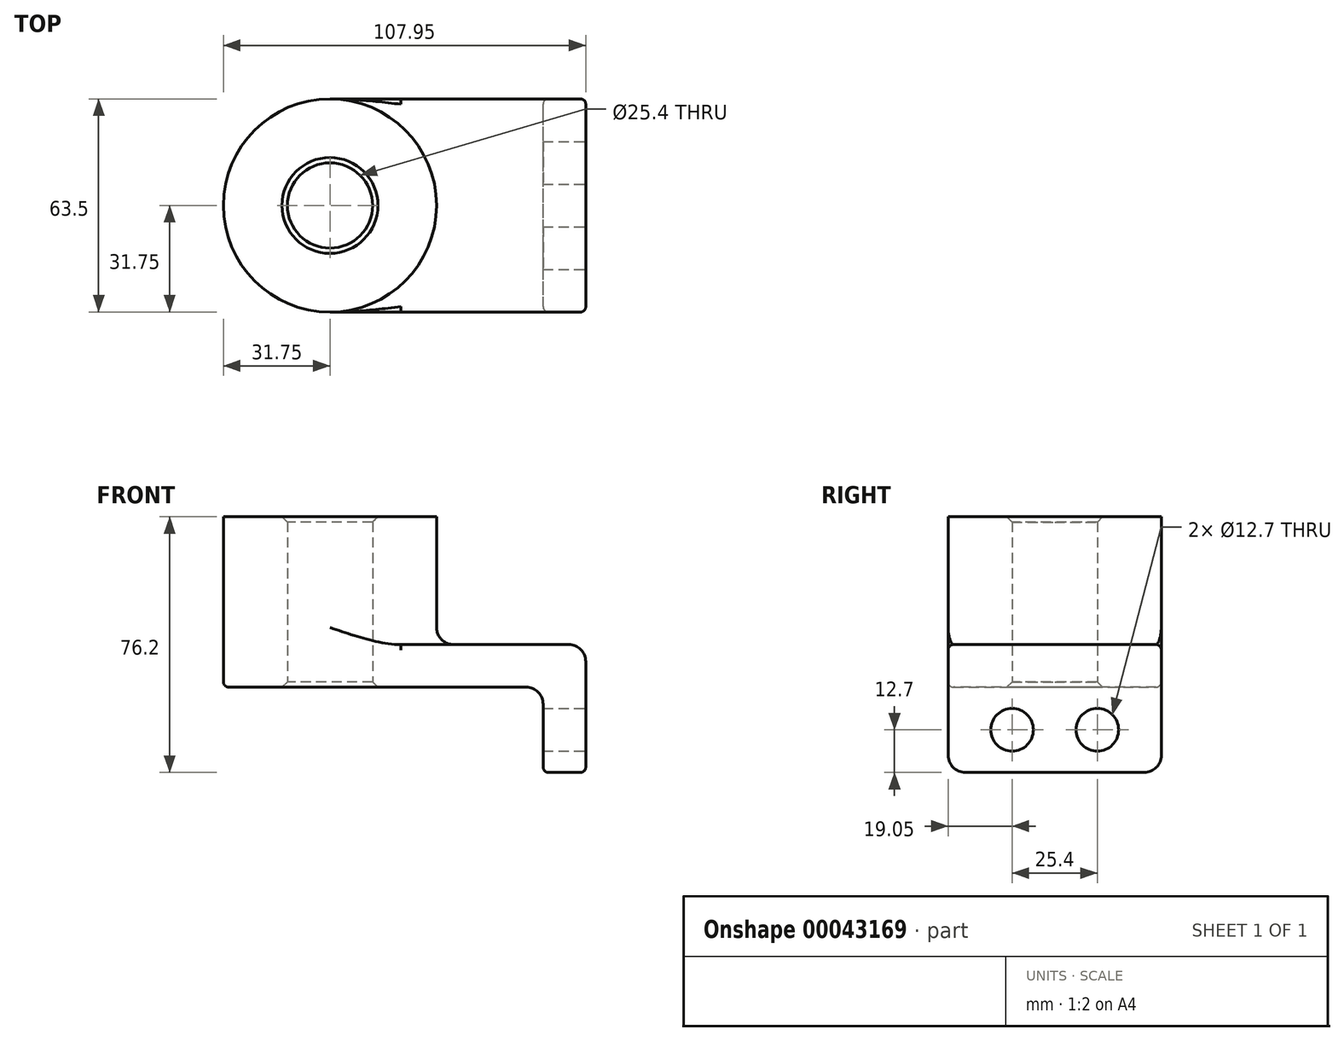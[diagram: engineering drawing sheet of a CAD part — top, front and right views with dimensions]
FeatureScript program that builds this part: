
annotation { "Feature Type Name" : "Feature", "Feature Type Description" : "" }
export const myFeature = defineFeature(function(context is Context, id is Id, definition is map)
    precondition{}
    {
        {
            var Q0;
            Q0=qCreatedBy(makeId("Top.planeOp"),FACE);
            var sketch = newSketch(context, id + "F0", { "sketchPlane" : qUnion([Q0])});
            skLineSegment(sketch, "E0.rect.bottom", {"start": v(-38.1, 31.75) * mm, "end": v(38.1, 31.75) * mm});
            skLineSegment(sketch, "E0.rect.top", {"start": v(-38.1, -31.75) * mm, "end": v(38.1, -31.75) * mm});
            skLineSegment(sketch, "E0.rect.left", {"start": v(-38.1, 31.75) * mm, "end": v(-38.1, -31.75) * mm});
            skLineSegment(sketch, "E0.rect.right", {"start": v(38.1, 31.75) * mm, "end": v(38.1, -31.75) * mm});
            skPoint(sketch, "E0.rect.middle", {"position": v(0, 0) * mm});
            skCircle(sketch, "E1", {"center": v(-38.1, 0) * mm, "radius": 31.75 * mm});
            skCircle(sketch, "E2", {"center": v(-38.1, 0) * mm, "radius": 12.7 * mm});
            skSolve(sketch);
        }
        {
            var Q0;
            Q0 = qSketchRegion(id + "F0", true);
            extrude(context, id + "F1", {"entities" : qUnion([Q0]), "depth" : 12.7 * mm});
        }
        {
            var Q0;
            {var subQ0=sQuery(id+"F0.wireOp",EDGE,"E2");var subQ1=sQuery(id+"F0.wireOp",EDGE,"E0.rect.left");var subQ3=makeQuery(id+"F0.imprint","INTERSECT",VERTEX,{"disambiguationData":[OD(0.0)],"derivedFrom":[subQ1,subQ0]});Q0=makeQuery(id+"F0.imprint","IMPRINT",FACE,{"disambiguationData":[TD([[makeQuery(id+"F0.imprint","IMPRINT",EDGE,{"disambiguationData":[TD([[subQ3,-1.0]])],"derivedFrom":subQ0}),-1.0]])]});}
            var Q1;
            {var subQ0=sQuery(id+"F0.wireOp",EDGE,"E2");var subQ1=sQuery(id+"F0.wireOp",EDGE,"E0.rect.left");var subQ3=makeQuery(id+"F0.imprint","INTERSECT",VERTEX,{"disambiguationData":[OD(0.0)],"derivedFrom":[subQ1,subQ0]});Q1=makeQuery(id+"F0.imprint","IMPRINT",FACE,{"disambiguationData":[TD([[makeQuery(id+"F0.imprint","IMPRINT",EDGE,{"disambiguationData":[TD([[subQ3,1.0]])],"derivedFrom":subQ0}),-1.0]])]});}
            extrude(context, id + "F2", {"entities" : qUnion([Q0, Q1]), "operationType" : NewBodyOperationType.ADD, "depth" : 50.8 * mm});
        }
        {
            var Q0;
            Q0=makeQuery(id+"F1.opExtrude","SWEPT_FACE",FACE,{"disambiguationData":[OSD([sQuery(id+"F0.wireOp",EDGE,"E0.rect.right")])]});
            var sketch = newSketch(context, id + "F3", { "sketchPlane" : qUnion([Q0])});
            skLineSegment(sketch, "E3.bottom", {"start": v(-31.75, 12.7) * mm, "end": v(31.75, 12.7) * mm});
            skLineSegment(sketch, "E3.top", {"start": v(-31.75, -25.4) * mm, "end": v(31.75, -25.4) * mm});
            skLineSegment(sketch, "E3.left", {"start": v(-31.75, 12.7) * mm, "end": v(-31.75, -25.4) * mm});
            skLineSegment(sketch, "E3.right", {"start": v(31.75, 12.7) * mm, "end": v(31.75, -25.4) * mm});
            skCircle(sketch, "E4", {"center": v(-12.7, -12.7) * mm, "radius": 6.35 * mm});
            skLineSegment(sketch, "E5", {"start": v(0, 0) * mm, "end": v(0, -25.4) * mm});
            skCircle(sketch, "E6.MirrorC", {"center": v(12.7, -12.7) * mm, "radius": 6.35 * mm});
            skSolve(sketch);
        }
        {
            var Q0;
            Q0 = qSketchRegion(id + "F3", true);
            extrude(context, id + "F4", {"entities" : qUnion([Q0]), "operationType" : NewBodyOperationType.ADD, "oppositeDirection" : true, "depth" : 12.7 * mm});
        }
        {
            var Q0;
            {var subQ0=sQuery(id+"F0.wireOp",EDGE,"E1");Q0=makeQuery(id+"F2.boolean.opBoolean","INTERSECT",EDGE,{"derivedFrom":[makeQuery(id+"F1.opExtrude","CAP_FACE",FACE,{"disambiguationData":[OSD([sQuery(id+"F0.wireOp",EDGE,"E0.rect.bottom"),sQuery(id+"F0.wireOp",EDGE,"E0.rect.top"),sQuery(id+"F0.wireOp",EDGE,"E0.rect.right"),subQ0,sQuery(id+"F0.wireOp",EDGE,"E2")])],"isStart":false}),makeQuery(id+"F2.opExtrude","SWEPT_FACE",FACE,{"disambiguationData":[OSD([subQ0])]})]});}
            var Q1;
            Q1=makeQuery(id+"F1.opExtrude","CAP_EDGE",EDGE,{"disambiguationData":[OSD([sQuery(id+"F0.wireOp",EDGE,"E0.rect.right")])],"isStart":false});
            var Q2;
            Q2=makeQuery(id+"F4.opExtrude","SWEPT_EDGE",EDGE,{"disambiguationData":[OSD([sQuery(id+"F3.wireOp",EDGE,"E3.top"),sQuery(id+"F3.wireOp",EDGE,"E3.right")])]});
            var Q3;
            Q3=makeQuery(id+"F4.opExtrude","SWEPT_EDGE",EDGE,{"disambiguationData":[OSD([sQuery(id+"F3.wireOp",EDGE,"E3.top"),sQuery(id+"F3.wireOp",EDGE,"E3.left")])]});
            var Q4;
            Q4=makeQuery(id+"F4.boolean.opBoolean","INTERSECT",EDGE,{"derivedFrom":[makeQuery(id+"F1.opExtrude","CAP_FACE",FACE,{"disambiguationData":[OSD([sQuery(id+"F0.wireOp",EDGE,"E0.rect.bottom"),sQuery(id+"F0.wireOp",EDGE,"E0.rect.top"),sQuery(id+"F0.wireOp",EDGE,"E0.rect.right"),sQuery(id+"F0.wireOp",EDGE,"E1"),sQuery(id+"F0.wireOp",EDGE,"E2")])],"isStart":true}),makeQuery(id+"F4.opExtrude","CAP_FACE",FACE,{"disambiguationData":[OSD([sQuery(id+"F3.wireOp",EDGE,"E3.bottom"),sQuery(id+"F3.wireOp",EDGE,"E3.top"),sQuery(id+"F3.wireOp",EDGE,"E3.left"),sQuery(id+"F3.wireOp",EDGE,"E3.right"),sQuery(id+"F3.wireOp",EDGE,"E4"),sQuery(id+"F3.wireOp",EDGE,"E6.MirrorC")])],"isStart":false})]});
            fillet(context, id + "F5", {"entities" : qUnion([Q0, Q1, Q2, Q3, Q4]), "radius" : 5.08 * mm, "tangentPropagation" : true, "allowEdgeOverflow" : false});
        }
        {
            var Q0;
            Q0=makeQuery(id+"F1.opExtrude","CAP_EDGE",EDGE,{"disambiguationData":[OSD([sQuery(id+"F0.wireOp",EDGE,"E0.rect.top")])],"isStart":false});
            var Q1;
            Q1=makeQuery(id+"F1.opExtrude","CAP_EDGE",EDGE,{"disambiguationData":[OSD([sQuery(id+"F0.wireOp",EDGE,"E0.rect.top")])],"isStart":true});
            fillet(context, id + "F6", {"entities" : qUnion([Q0, Q1]), "radius" : 1.59 * mm, "tangentPropagation" : true, "allowEdgeOverflow" : false});
        }
        {
            var Q0;
            {var subQ0=sQuery(id+"F0.wireOp",EDGE,"E2");Q0=makeQuery(id+"F2.boolean.opBoolean","MERGE",FACE,{"derivedFrom":[makeQuery(id+"F1.opExtrude","SWEPT_FACE",FACE,{"disambiguationData":[OSD([subQ0])]}),makeQuery(id+"F2.opExtrude","SWEPT_FACE",FACE,{"disambiguationData":[OSD([subQ0])]})]});}
            chamfer(context, id + "F7", {"entities" : qUnion([Q0]), "width" : 1.59 * mm, "tangentPropagation" : true});
        }
    });
